# Revit family: Interceptor_Oil_Large_Capacity-Zurn-Z1188-ST
name_source: partatom
category: Plumbing Fixtures
units: mm (PartAtom-declared; Revit-internal decimal feet)

## family parameters
Always vertical = Yes
Cut with Voids When Loaded = No
Maintain Annotation Orientation = No
OmniClass Number = 23.45.30.00
OmniClass Title = Washing and Waste Disposal Equipment
Part Type = Normal
Room Calculation Point = No
Round Connector Dimension = Use Radius
Shared = No
Work Plane-Based = No

## types (11) — shared parameters
Assembly Code = D2090300
CW Connection = No
Default Elevation = 25 "
Description = LARGE CAPACITY OIL INTERCEPTOR W/ INTEGRAL STORAGE TANK
Extension Box Width = 4.25 "
Extented Box Length = 9.25 "
HW Connection = No
Main Material = Steel - Zurn - Fabricated - Acid resistant Coated
Manufacturer = Zurn Water, LLC
Manufacurer Brand = Zurn
Model = Z1188-ST
Modified Date = 12/26/2025
Product Documentation Link = https://files.zurn.com
Product Installation Sheet URL = https://files.zurn.com
Product Page URL = https://www.zurn.com
Product data url = https://www.bimobject.com
Sanitary Radius = 1 "
URL = www.zurn.com
Vent Connection = No
Vent Radius = 1 "
WFU = 1
Waste Connection = Yes
zero-valued in all types: CWFU, HWFU

## per-type parameters (varying)
| type | Approx. Weight (Lbs) | Center Lenght of G | Dimension (H) | Dimension (J) | Height of Body (C) | Inlet/Outlet (D/E) | Inlet/Outlet Connetor Radius | Inlet/Outlet Radius (Actual) | Inlet/Outlet Radius (Inner) | No.of Covers | Overall Length (F) | Type Comments | Water Capacity Gal (L) | Width of Body (G) |
| Z1188-ST-75 G.P.M-3" | 615 " | 14.313 " | 29.25 " | 15.5 " | 22.75 " | 18.5 " | 1.5 " | 1.75 " | 1.534 " | 1 " | 51.375 " | Z1188-ST-75 G.P.M-3 Inch Outlet | 88 " | 65.375 " |
| Z1188-ST-100 G.P.M-3" | 800 " | 16.813 " | 35.25 " | 19.75 " | 27 " | 23 " | 1.5 " | 1.75 " | 1.534 " | 1 " | 60.375 " | Z1188-ST-100 G.P.M-3 Inch Outlet | 159 " | 82.375 " |
| Z1188-ST-125 G.P.M-3" | 1450 " | 20 " | 36 " | 21 " | 30.125 " | 24.5 " | 1.5 " | 1.75 " | 1.534 " | 2 " | 64.25 " | Z1188-ST-125 G.P.M-3 Inch Outlet | 208 " | 84.625 " |
| Z1188-ST-150 G.P.M-4" | 1640 " | 20.813 " | 38.688 " | 21.625 " | 30.75 " | 25.25 " | 2 " | 2.25 " | 2.013 " | 2 " | 68.25 " | Z1188-ST-150 G.P.M-4 Inch Outlet | 235 " | 82.75 " |
| Z1188-ST-200 G.P.M-4" | 1950 " | 21.813 " | 43.5 " | 26.375 " | 35.5 " | 29.875 " | 2 " | 2.25 " | 2.013 " | 2 " | 71.375 " | Z1188-ST-200 G.P.M-4 Inch Outlet | 333 " | 92.75 " |
| Z1188-ST-250 G.P.M-5" | 2650 " | 25.813 " | 40.75 " | 32.5 " | 41 " | 36 " | 2.5 " | 2.782 " | 2.524 " | 2 " | 75.5 " | Z1188-ST-250 G.P.M-5 Inch Outlet | 445 " | 95.625 " |
| Z1188-ST-300 G.P.M-5" | 3400 " | 29.313 " | 48.006 " | 37.75 " | 46.25 " | 39.625 " | 2.5 " | 2.782 " | 2.524 " | 2 " | 82.375 " | Z1188-ST-300 G.P.M-5 Inch Outlet | 664 " | 92.375 " |
| Z1188-ST-350 G.P.M-6" | 4000 " | 31.313 " | 61.938 " | 40.375 " | 50.5 " | 43.875 " | 3 " | 3.313 " | 3.033 " | 2 " | 103.125 " | Z1188-ST-350 G.P.M-6 Inch Outlet | 1006 " | 104.75 " |
| Z1188-ST-400 G.P.M-6" | 4700 " | 33.5 " | 66.563 " | 44.125 " | 54.25 " | 47.625 " | 3 " | 3.313 " | 3.033 " | 2 " | 110.125 " | Z1188-ST-400 G.P.M-6 Inch Outlet | 1266 " | 102.625 " |
| Z1188-ST-450 G.P.M-6" | 5200 " | 36 " | 75.25 " | 44.625 " | 55.25 " | 48.625 " | 3 " | 3.313 " | 3.033 " | 2 " | 123.125 " | Z1188-ST-450 G.P.M-6 Inch Outlet | 1575 " | 102.875 " |
| Z1188-ST-500 G.P.M-6" | 5500 " | 37 " | 73.938 " | 48.125 " | 57.25 " | 51.652 " | 3 " | 3.313 " | 3.033 " | 2 " | 124.125 " | Z1188-ST-500 G.P.M-6 Inch Outlet | 1695 " | 103.625 " |

## geometry (parser evidence)
native form markers: Sweep x6
no freeform markers — native parametric forms only
